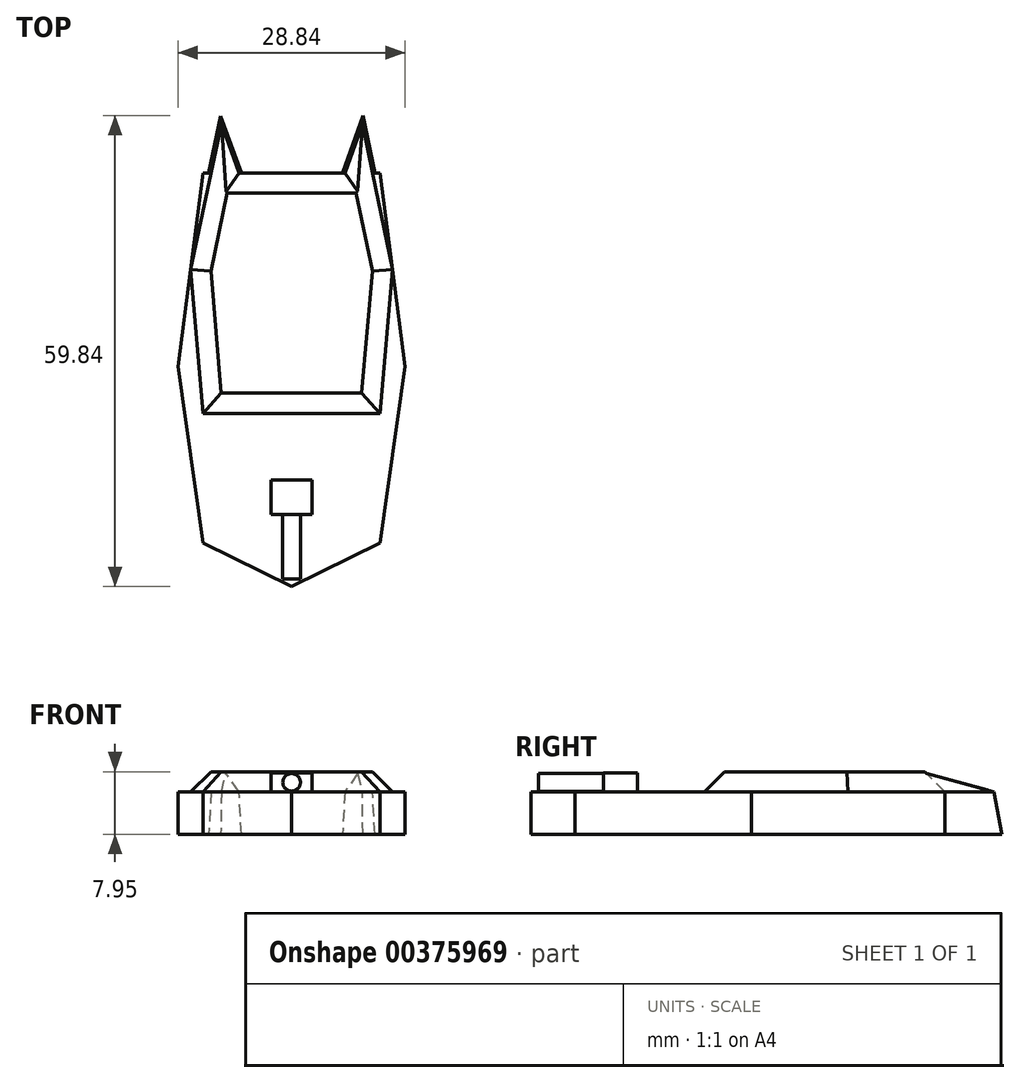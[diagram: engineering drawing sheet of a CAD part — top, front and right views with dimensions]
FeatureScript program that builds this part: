
annotation { "Feature Type Name" : "Feature", "Feature Type Description" : "" }
export const myFeature = defineFeature(function(context is Context, id is Id, definition is map)
    precondition{}
    {
        {
            var Q0;
            Q0=qCreatedBy(makeId("Top.planeOp"),FACE);
            var sketch = newSketch(context, id + "F0", { "sketchPlane" : qUnion([Q0])});
            skLineSegment(sketch, "E0", {"start": v(0, 16.38) * mm, "end": v(-7.5, 16.38) * mm});
            skLineSegment(sketch, "E1", {"start": v(-7.5, 16.38) * mm, "end": v(-9.61, 0) * mm});
            skLineSegment(sketch, "E2", {"start": v(-9.61, 0) * mm, "end": v(-7.5, -14.95) * mm});
            skLineSegment(sketch, "E3", {"start": v(-7.5, -14.95) * mm, "end": v(0, -18.66) * mm});
            skLineSegment(sketch, "E4", {"start": v(0, -18.66) * mm, "end": v(7.5, -14.95) * mm});
            skLineSegment(sketch, "E5", {"start": v(7.5, -14.95) * mm, "end": v(9.61, 0) * mm});
            skLineSegment(sketch, "E6", {"start": v(9.61, 0) * mm, "end": v(7.5, 16.38) * mm});
            skLineSegment(sketch, "E7", {"start": v(7.5, 16.38) * mm, "end": v(0, 16.38) * mm});
            skSolve(sketch);
        }
        {
            var Q0;
            Q0=makeQuery(id+"F0.imprint","IMPRINT",FACE,{"disambiguationData":[TD([[makeQuery(id+"F0.imprint","IMPRINT",EDGE,{"derivedFrom":sQuery(id+"F0.wireOp",EDGE,"E0")}),1.0]])]});
            extrude(context, id + "F1", {"entities" : qUnion([Q0]), "depth" : 3.6 * mm});
        }
        {
            var Q0;
            Q0=makeQuery(id+"F1.opExtrude","CAP_FACE",FACE,{"disambiguationData":[OSD([sQuery(id+"F0.wireOp",EDGE,"E0"),sQuery(id+"F0.wireOp",EDGE,"E1"),sQuery(id+"F0.wireOp",EDGE,"E2"),sQuery(id+"F0.wireOp",EDGE,"E3"),sQuery(id+"F0.wireOp",EDGE,"E4"),sQuery(id+"F0.wireOp",EDGE,"E5"),sQuery(id+"F0.wireOp",EDGE,"E6"),sQuery(id+"F0.wireOp",EDGE,"E7")])],"isStart":false});
            var sketch = newSketch(context, id + "F2", { "sketchPlane" : qUnion([Q0])});
            skLineSegment(sketch, "E8", {"start": v(-5.95, 20.53) * mm, "end": v(-8.56, 8.19) * mm});
            skLineSegment(sketch, "E9", {"start": v(-8.56, 8.19) * mm, "end": v(-7.51, -3.98) * mm});
            skLineSegment(sketch, "E10", {"start": v(-7.51, -3.98) * mm, "end": v(7.49, -3.98) * mm});
            skLineSegment(sketch, "E11", {"start": v(7.49, -3.98) * mm, "end": v(8.56, 8.19) * mm});
            skLineSegment(sketch, "E12", {"start": v(8.56, 8.19) * mm, "end": v(5.99, 20.53) * mm});
            skLineSegment(sketch, "E13", {"start": v(5.99, 20.53) * mm, "end": v(4.5, 16.38) * mm});
            skLineSegment(sketch, "E14", {"start": v(4.5, 16.38) * mm, "end": v(-4.45, 16.38) * mm});
            skLineSegment(sketch, "E15", {"start": v(-5.95, 20.53) * mm, "end": v(-4.45, 16.38) * mm});
            skPoint(sketch, "E16", {"position": v(8.56, 8.19) * mm});
            skSolve(sketch);
        }
        {
            var Q0;
            {var subQ1=sQuery(id+"F2.wireOp",EDGE,"E9");Q0=makeQuery(id+"F2.imprint","IMPRINT",FACE,{"disambiguationData":[TD([[makeQuery(id+"F2.imprint","IMPRINT",EDGE,{"derivedFrom":subQ1}),1.0]])]});}
            var Q1;
            {var subQ0=sQuery(id+"F2.wireOp",EDGE,"E13");Q1=makeQuery(id+"F2.imprint","IMPRINT",FACE,{"disambiguationData":[TD([[makeQuery(id+"F2.imprint","IMPRINT",EDGE,{"derivedFrom":subQ0}),1.0]])]});}
            var Q2;
            {var subQ0=sQuery(id+"F2.wireOp",EDGE,"E15");Q2=makeQuery(id+"F2.imprint","IMPRINT",FACE,{"disambiguationData":[TD([[makeQuery(id+"F2.imprint","IMPRINT",EDGE,{"derivedFrom":subQ0}),-1.0]])]});}
            extrude(context, id + "F3", {"entities" : qUnion([Q0, Q1, Q2]), "operationType" : NewBodyOperationType.ADD, "depth" : 1.7 * mm, "hasDraft" : true, "draftAngle" : 45 * degree, "draftPullDirection" : true});
        }
        {
            var Q0;
            {var subQ0=sQuery(id+"F2.wireOp",EDGE,"E8");var subQ3=sQuery(id+"F2.wireOp",EDGE,"E14");var subQ4=sQuery(id+"F2.wireOp",EDGE,"E15");Q0=makeQuery(id+"F3.boolean.opBoolean","SPLIT",FACE,{"disambiguationData":[TD([makeQuery(id+"F3.opExtrude","SWEPT_FACE",FACE,{"disambiguationData":[OSD([subQ0])]})])],"derivedFrom":makeQuery(id+"F3.opExtrude","CAP_FACE",FACE,{"disambiguationData":[OSD([subQ0,sQuery(id+"F2.wireOp",EDGE,"E9"),sQuery(id+"F2.wireOp",EDGE,"E10"),sQuery(id+"F2.wireOp",EDGE,"E11"),sQuery(id+"F2.wireOp",EDGE,"E12"),sQuery(id+"F2.wireOp",EDGE,"E13"),subQ3,subQ4])],"isStart":true})});}
            var Q1;
            {var subQ0=sQuery(id+"F2.wireOp",EDGE,"E13");var subQ1=sQuery(id+"F2.wireOp",EDGE,"E12");var subQ4=sQuery(id+"F2.wireOp",EDGE,"E14");Q1=makeQuery(id+"F3.boolean.opBoolean","SPLIT",FACE,{"disambiguationData":[TD([makeQuery(id+"F3.opExtrude","SWEPT_FACE",FACE,{"disambiguationData":[OSD([subQ1])]})])],"derivedFrom":makeQuery(id+"F3.opExtrude","CAP_FACE",FACE,{"disambiguationData":[OSD([sQuery(id+"F2.wireOp",EDGE,"E8"),sQuery(id+"F2.wireOp",EDGE,"E9"),sQuery(id+"F2.wireOp",EDGE,"E10"),sQuery(id+"F2.wireOp",EDGE,"E11"),subQ1,subQ0,subQ4,sQuery(id+"F2.wireOp",EDGE,"E15")])],"isStart":true})});}
            extrude(context, id + "F4", {"entities" : qUnion([Q0, Q1]), "operationType" : NewBodyOperationType.ADD, "depth" : 3.6 * mm, "hasDraft" : true, "draftAngle" : 3 * degree});
        }
        {
            var Q0;
            {var subQ0=sQuery(id+"F0.wireOp",EDGE,"E6");var subQ1=sQuery(id+"F0.wireOp",EDGE,"E5");var subQ2=sQuery(id+"F0.wireOp",EDGE,"E4");var subQ3=sQuery(id+"F0.wireOp",EDGE,"E2");var subQ4=sQuery(id+"F0.wireOp",EDGE,"E3");var subQ5=sQuery(id+"F0.wireOp",EDGE,"E1");var subQ6=makeQuery(id+"F1.opExtrude","CAP_FACE",FACE,{"disambiguationData":[OSD([sQuery(id+"F0.wireOp",EDGE,"E0"),subQ5,subQ3,subQ4,subQ2,subQ1,subQ0,sQuery(id+"F0.wireOp",EDGE,"E7")])],"isStart":false});Q0=makeQuery(id+"F3.boolean.opBoolean","SPLIT",FACE,{"disambiguationData":[TD([subQ6,makeQuery(id+"F1.opExtrude","SWEPT_FACE",FACE,{"disambiguationData":[OSD([subQ5])]}),makeQuery(id+"F1.opExtrude","SWEPT_FACE",FACE,{"disambiguationData":[OSD([subQ3])]}),makeQuery(id+"F1.opExtrude","SWEPT_FACE",FACE,{"disambiguationData":[OSD([subQ4])]}),makeQuery(id+"F1.opExtrude","SWEPT_FACE",FACE,{"disambiguationData":[OSD([subQ2])]}),makeQuery(id+"F1.opExtrude","SWEPT_FACE",FACE,{"disambiguationData":[OSD([subQ1])]}),makeQuery(id+"F1.opExtrude","SWEPT_FACE",FACE,{"disambiguationData":[OSD([subQ0])]}),makeQuery(id+"F3.opExtrude","SWEPT_FACE",FACE,{"disambiguationData":[OSD([sQuery(id+"F2.wireOp",EDGE,"E8")])]}),makeQuery(id+"F3.opExtrude","SWEPT_FACE",FACE,{"disambiguationData":[OSD([sQuery(id+"F2.wireOp",EDGE,"E9")])]}),makeQuery(id+"F3.opExtrude","SWEPT_FACE",FACE,{"disambiguationData":[OSD([sQuery(id+"F2.wireOp",EDGE,"E10")])]}),makeQuery(id+"F3.opExtrude","SWEPT_FACE",FACE,{"disambiguationData":[OSD([sQuery(id+"F2.wireOp",EDGE,"E11")])]}),makeQuery(id+"F3.opExtrude","SWEPT_FACE",FACE,{"disambiguationData":[OSD([sQuery(id+"F2.wireOp",EDGE,"E12")])]})])],"derivedFrom":subQ6});}
            var sketch = newSketch(context, id + "F5", { "sketchPlane" : qUnion([Q0])});
            skLineSegment(sketch, "E17.bottom", {"start": v(-1.72, -9.63) * mm, "end": v(1.72, -9.63) * mm});
            skLineSegment(sketch, "E17.top", {"start": v(-1.72, -12.53) * mm, "end": v(1.72, -12.53) * mm});
            skLineSegment(sketch, "E17.left", {"start": v(-1.72, -9.63) * mm, "end": v(-1.72, -12.53) * mm});
            skLineSegment(sketch, "E17.right", {"start": v(1.72, -9.63) * mm, "end": v(1.72, -12.53) * mm});
            skPoint(sketch, "E17.middle", {"position": v(0, -11.08) * mm});
            skSolve(sketch);
        }
        {
            var Q0;
            Q0 = qSketchRegion(id + "F5", true);
            extrude(context, id + "F6", {"entities" : qUnion([Q0]), "operationType" : NewBodyOperationType.ADD, "depth" : 1.6 * mm});
        }
        {
            var Q0;
            Q0=makeQuery(id+"F6.opExtrude","SWEPT_FACE",FACE,{"disambiguationData":[OSD([sQuery(id+"F5.wireOp",EDGE,"E17.top")])]});
            var sketch = newSketch(context, id + "F7", { "sketchPlane" : qUnion([Q0])});
            skCircle(sketch, "E18", {"center": v(0, 4.4) * mm, "radius": 0.75 * mm});
            skSolve(sketch);
        }
        {
            var Q0;
            Q0=makeQuery(id+"F7.imprint","IMPRINT",FACE,{"disambiguationData":[TD([[makeQuery(id+"F7.imprint","IMPRINT",EDGE,{"derivedFrom":sQuery(id+"F7.wireOp",EDGE,"E18")}),1.0]])]});
            extrude(context, id + "F8", {"entities" : qUnion([Q0]), "operationType" : NewBodyOperationType.ADD, "depth" : 5.5 * mm});
        }
        {
            var Q0;
            Q0=makeQuery(id+"F1.opExtrude","SWEPT_BODY",BODY,{"disambiguationData":[OSD([sQuery(id+"F0.wireOp",EDGE,"E0"),sQuery(id+"F0.wireOp",EDGE,"E1"),sQuery(id+"F0.wireOp",EDGE,"E2"),sQuery(id+"F0.wireOp",EDGE,"E3"),sQuery(id+"F0.wireOp",EDGE,"E4"),sQuery(id+"F0.wireOp",EDGE,"E5"),sQuery(id+"F0.wireOp",EDGE,"E6"),sQuery(id+"F0.wireOp",EDGE,"E7")])]});
            var Q1;
            Q1=qCreatedBy(makeId("Origin.pointOp"),VERTEX);
            transform(context, id + "F9", {"entities" : qUnion([Q0]), "transformType" : TransformType.SCALE_UNIFORMLY, "scale" : 1.5, "scalePoint" : qUnion([Q1]), "makeCopy" : false});
        }
    });
